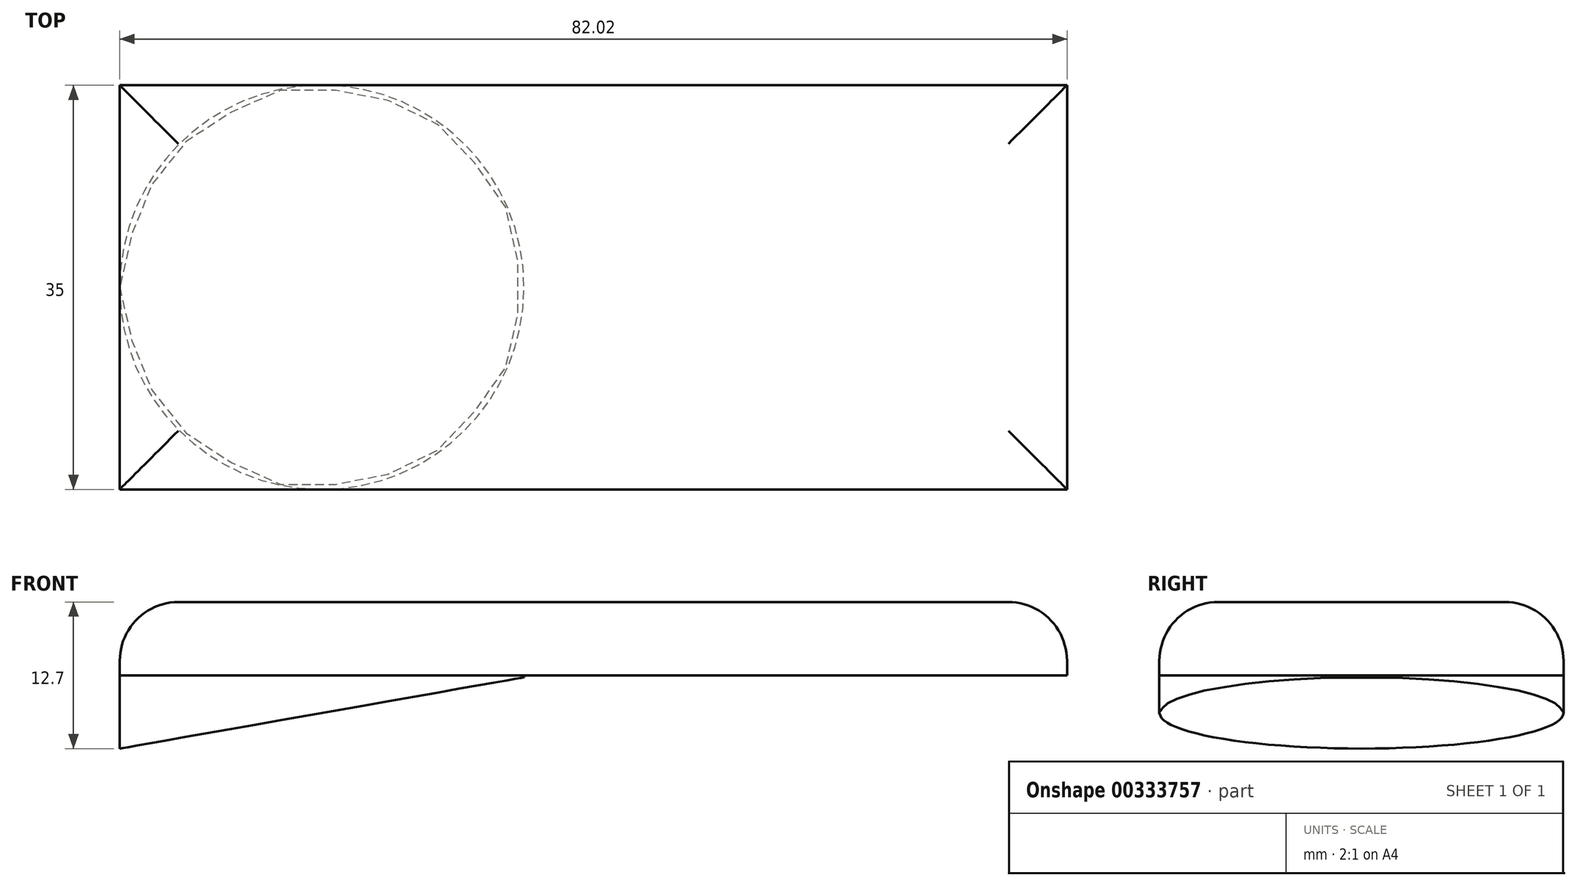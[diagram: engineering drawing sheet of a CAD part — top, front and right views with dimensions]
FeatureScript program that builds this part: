
annotation { "Feature Type Name" : "Feature", "Feature Type Description" : "" }
export const myFeature = defineFeature(function(context is Context, id is Id, definition is map)
    precondition{}
    {
        {
            var Q0;
            Q0=qCreatedBy(makeId("Top.planeOp"),FACE);
            var sketch = newSketch(context, id + "F0", { "sketchPlane" : qUnion([Q0])});
            skCircle(sketch, "E0", {"center": v(0, 0) * mm, "radius": 17.5 * mm});
            skSolve(sketch);
        }
        {
            var Q0;
            Q0 = qSketchRegion(id + "F0", true);
            extrude(context, id + "F1", {"entities" : qUnion([Q0]), "depth" : 6.35 * mm});
        }
        {
            var Q0;
            Q0=qCreatedBy(makeId("Front.planeOp"),FACE);
            var sketch = newSketch(context, id + "F2", { "sketchPlane" : qUnion([Q0])});
            skLineSegment(sketch, "E1", {"start": v(0, 0) * mm, "end": v(-17.5, 0) * mm});
            skLineSegment(sketch, "E2", {"start": v(17.5, 0) * mm, "end": v(0, 0) * mm});
            skLineSegment(sketch, "E3", {"start": v(17.5, 0) * mm, "end": v(17.5, 6.17) * mm});
            skLineSegment(sketch, "E4", {"start": v(-17.5, 0) * mm, "end": v(17.5, 6.17) * mm});
            skSolve(sketch);
        }
        {
            var Q0;
            Q0 = qSketchRegion(id + "F2", true);
            extrude(context, id + "F3", {"entities" : qUnion([Q0]), "operationType" : NewBodyOperationType.REMOVE, "depth" : 25.4 * mm, "hasSecondDirection" : true, "secondDirectionOppositeDirection" : true, "secondDirectionDepth" : 25.4 * mm});
        }
        {
            var Q0;
            Q0=makeQuery(id+"F1.opExtrude","CAP_FACE",FACE,{"disambiguationData":[OSD([sQuery(id+"F0.wireOp",EDGE,"E0")])],"isStart":false});
            var sketch = newSketch(context, id + "F4", { "sketchPlane" : qUnion([Q0])});
            skPoint(sketch, "E5.middle", {"position": v(0, 0) * mm});
            skLineSegment(sketch, "E6.right", {"start": v(-17.5, 17.5) * mm, "end": v(-17.5, -17.5) * mm});
            skLineSegment(sketch, "E7", {"start": v(-17.5, 17.5) * mm, "end": v(64.52, 17.5) * mm});
            skLineSegment(sketch, "E8", {"start": v(64.52, 17.5) * mm, "end": v(64.52, -17.5) * mm});
            skLineSegment(sketch, "E9", {"start": v(64.52, -17.5) * mm, "end": v(-17.5, -17.5) * mm});
            skSolve(sketch);
        }
        {
            var Q0;
            Q0 = qSketchRegion(id + "F4", true);
            extrude(context, id + "F5", {"entities" : qUnion([Q0]), "operationType" : NewBodyOperationType.ADD, "depth" : 6.35 * mm});
        }
        {
            var Q0;
            Q0=makeQuery(id+"F5.opExtrude","CAP_FACE",FACE,{"disambiguationData":[OSD([sQuery(id+"F4.wireOp",EDGE,"E6.right"),sQuery(id+"F4.wireOp",EDGE,"E7"),sQuery(id+"F4.wireOp",EDGE,"E8"),sQuery(id+"F4.wireOp",EDGE,"E9")])],"isStart":false});
            fillet(context, id + "F6", {"entities" : qUnion([Q0]), "radius" : 5.08 * mm, "tangentPropagation" : true, "allowEdgeOverflow" : false});
        }
    });
